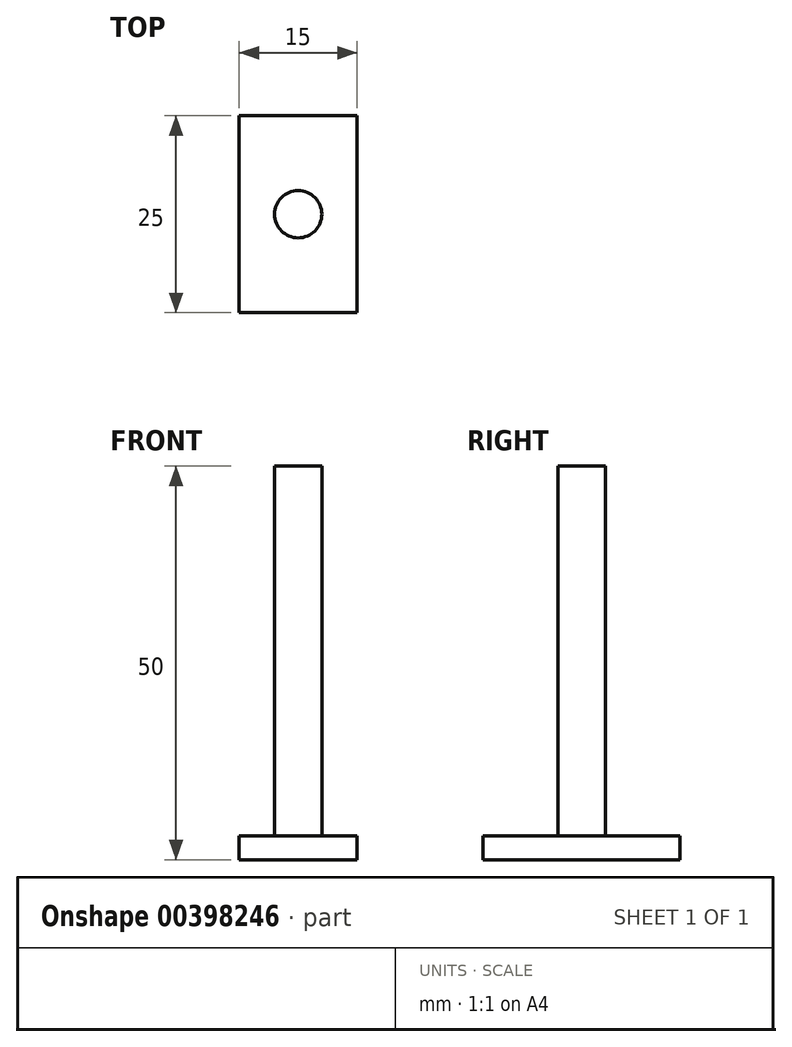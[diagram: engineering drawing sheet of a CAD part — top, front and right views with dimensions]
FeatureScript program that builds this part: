
annotation { "Feature Type Name" : "Feature", "Feature Type Description" : "" }
export const myFeature = defineFeature(function(context is Context, id is Id, definition is map)
    precondition{}
    {
        {
            var Q0;
            Q0=qCreatedBy(makeId("Top.planeOp"),FACE);
            var sketch = newSketch(context, id + "F0", { "sketchPlane" : qUnion([Q0])});
            skLineSegment(sketch, "E0.bottom", {"start": v(7.5, 12.5) * mm, "end": v(-7.5, 12.5) * mm});
            skLineSegment(sketch, "E0.top", {"start": v(7.5, -12.5) * mm, "end": v(-7.5, -12.5) * mm});
            skLineSegment(sketch, "E0.left", {"start": v(7.5, 12.5) * mm, "end": v(7.5, -12.5) * mm});
            skLineSegment(sketch, "E0.right", {"start": v(-7.5, 12.5) * mm, "end": v(-7.5, -12.5) * mm});
            skPoint(sketch, "E0.middle", {"position": v(0, 0) * mm});
            skText(sketch, "E1", { "text": "יקנ", "fontName": "Arimo-Regular.ttf"});
            const initialGuessF0  = {"E1": [-0.0207, -0.00968, 1, 0, 0.00586]};
            skSetInitialGuess(sketch, initialGuessF0);
            skSolve(sketch);
        }
        {
            var Q0;
            Q0=makeQuery(id+"F0.imprint","IMPRINT",FACE,{"disambiguationData":[TD([[makeQuery(id+"F0.imprint","IMPRINT",EDGE,{"derivedFrom":sQuery(id+"F0.wireOp",EDGE,"gj2cnrTZ-Nbdh-3dZZ-qGeT-8HNVyAAyzp4e")}),1.0]])]});
            var Q1;
            Q1=makeQuery(id+"F0.imprint","IMPRINT",FACE,{"disambiguationData":[TD([[makeQuery(id+"F0.imprint","IMPRINT",EDGE,{"derivedFrom":sQuery(id+"F0.wireOp",EDGE,"E0.bottom")}),1.0]])]});
            extrude(context, id + "F1", {"entities" : qUnion([Q0, Q1]), "depth" : 3 * mm});
        }
        {
            var Q0;
            Q0=qCreatedBy(makeId("Top.planeOp"),FACE);
            var sketch = newSketch(context, id + "F2", { "sketchPlane" : qUnion([Q0])});
            skCircle(sketch, "E2", {"center": v(0, 0) * mm, "radius": 3 * mm});
            skSolve(sketch);
        }
        {
            var Q0;
            Q0 = qSketchRegion(id + "F2", true);
            extrude(context, id + "F3", {"entities" : qUnion([Q0]), "operationType" : NewBodyOperationType.ADD, "depth" : 50 * mm});
        }
    });
